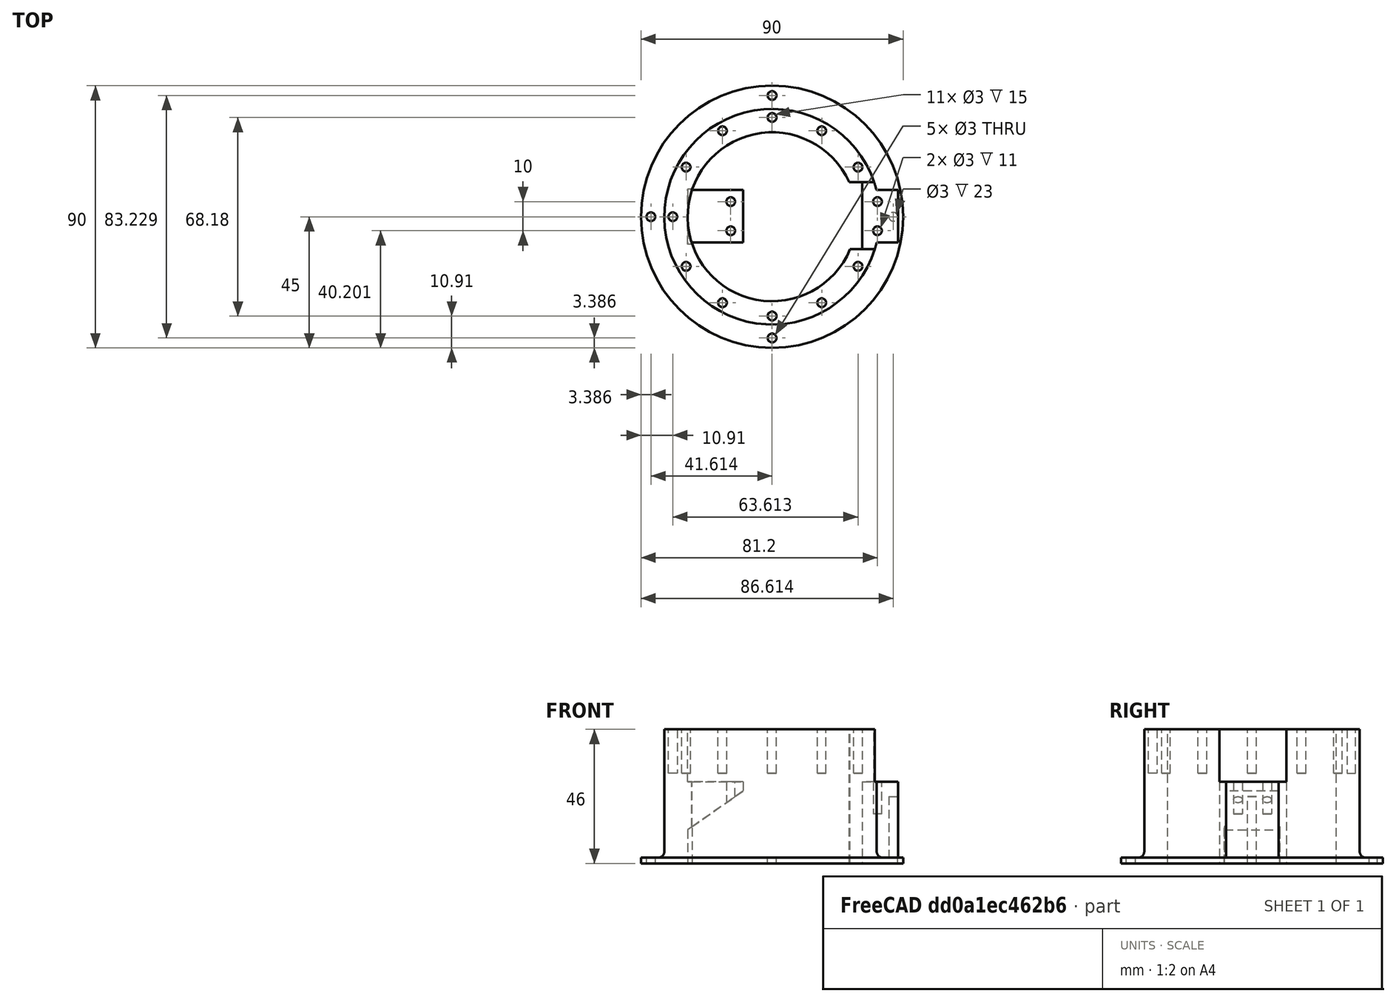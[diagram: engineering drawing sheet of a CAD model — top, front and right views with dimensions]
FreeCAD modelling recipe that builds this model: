
FCSTD DOCUMENT  (FreeCAD 0.20R29177 +426 (Git))
Label: servo_mount_container
License: All rights reserved
LicenseURL: http://en.wikipedia.org/wiki/All_rights_reserved
objects: Sketcher::SketchObject×9, PartDesign::Pocket×6, PartDesign::Pad×3, Mesh::Feature×2, PartDesign::PolarPattern×2, PartDesign::Fillet×1, PartDesign::Body×1
note: 32 computed .brp shape members not serialized (recipe doc carries the construction recipe); baked Part::Feature solids carry a one-line shape summary decoded from their .brp

FEATURE [Mesh::Feature] MG996R_body  label="MG996R-body"
  Placement = pos=(-4,-12,0) rot=(0,1,0;1.5708rad)
FEATURE [Sketcher::SketchObject] Sketch001  label="servo_screw_support"
  AttachmentOffset = pos=(0,0,5) rot=(0,0,1;0rad)
  FullyConstrained = false
  MapMode = 5
  Placement = pos=(0,0,5) rot=(0,0,1;0rad)
  Support = -> [XY_Plane]
  sketch-geometry (4):
    g0: LineSegment StartX=-31.783 StartY=9.16249 StartZ=0 EndX=43.217 EndY=9.16249 EndZ=0
    g1: LineSegment StartX=43.217 StartY=9.16249 StartZ=0 EndX=43.217 EndY=-8.83751 EndZ=0
    g2: LineSegment StartX=43.217 StartY=-8.83751 StartZ=0 EndX=-31.783 EndY=-8.83751 EndZ=0
    g3: LineSegment StartX=-31.783 StartY=-8.83751 StartZ=0 EndX=-31.783 EndY=9.16249 EndZ=0
  constraints (9):
    c: Coincident(g0,g1)
    c: Coincident(g1,g2)
    c: Coincident(g2,g3)
    c: Coincident(g3,g0)
    c: Horizontal(g0)
    c: Horizontal(g2)
    c: Vertical(g1)
    c: DistanceX(g0,g0) = 75
    c: DistanceY(g3,g3) = 18
FEATURE [PartDesign::Pad] Pad  label="servo_support_pad"
  Direction = (0,0,1)
  Length = 28
  Length2 = 10
  Profile = -> Sketch001
  ReferenceAxis = -> Sketch001 [N_Axis]
  Reversed = true
  Type = 0
FEATURE [Mesh::Feature] OuterRace
  Placement = pos=(0,0,32) rot=(0,0,1;0rad)
FEATURE [Sketcher::SketchObject] Sketch004  label="servo_body_insert"
  FullyConstrained = false
  MapMode = 5
  Support = -> [XY_Plane]
  sketch-geometry (4):
    g0: LineSegment StartX=-10 StartY=11.8586 StartZ=0 EndX=31 EndY=11.8586 EndZ=0
    g1: LineSegment StartX=31 StartY=11.8586 StartZ=0 EndX=31 EndY=-11.1414 EndZ=0
    g2: LineSegment StartX=31 StartY=-11.1414 StartZ=0 EndX=-10 EndY=-11.1414 EndZ=0
    g3: LineSegment StartX=-10 StartY=-11.1414 StartZ=0 EndX=-10 EndY=11.8586 EndZ=0
  constraints (11):
    c: Coincident(g0,g1)
    c: Coincident(g1,g2)
    c: Coincident(g2,g3)
    c: Coincident(g3,g0)
    c: Horizontal(g0)
    c: Horizontal(g2)
    c: Vertical(g1)
    c: Vertical(g3)
    c: DistanceX(g0,g0) = 41
    c: DistanceY(g3,g3) = 23
    c: DistanceX(g2,g-1) = 10
FEATURE [Sketcher::SketchObject] Sketch005  label="servo_screw_holes_support"
  AttachmentOffset = pos=(0,0,5) rot=(0,0,1;0rad)
  ExternalGeometry = -> [Sketch004,Sketch001]
  FullyConstrained = false
  MapMode = 5
  Placement = pos=(0,0,5) rot=(0,0,1;0rad)
  Support = -> [XY_Plane]
  sketch-geometry (4):
    g0: LineSegment StartX=31 StartY=11.8586 StartZ=0 EndX=40.0382 EndY=11.8586 EndZ=0
    g1: LineSegment StartX=40.0382 StartY=11.8586 StartZ=0 EndX=40.0382 EndY=-11.1414 EndZ=0
    g2: LineSegment StartX=40.0382 StartY=-11.1414 StartZ=0 EndX=31 EndY=-11.1414 EndZ=0
    g3: LineSegment StartX=31 StartY=-11.1414 StartZ=0 EndX=31 EndY=11.8586 EndZ=0
  constraints (10):
    c: Coincident(g0,g1)
    c: Coincident(g1,g2)
    c: Coincident(g2,g3)
    c: Coincident(g3,g0)
    c: Horizontal(g0)
    c: Horizontal(g2)
    c: Vertical(g1)
    c: Vertical(g3)
    c: Coincident(g0,g-3)
    c: DistanceY(g1,g1) = 23
FEATURE [Sketcher::SketchObject] Sketch006  label="slew_outer_screw_holes"
  AttachmentOffset = pos=(0,0,23) rot=(0,0,1;0rad)
  FullyConstrained = true
  MapMode = 5
  Placement = pos=(0,0,23) rot=(0,0,1;0rad)
  Support = -> [XY_Plane]
  sketch-geometry (1):
    g0: Circle CenterX=-34.09 CenterY=0 CenterZ=0 NormalX=0 NormalY=0 NormalZ=1 AngleXU=0 Radius=1.5
  constraints (3):
    c: PointOnObject(g0,g-1)
    c: Radius(g0) = 1.5
    c: DistanceX(g0,g-1) = 34.09
FEATURE [Sketcher::SketchObject] Sketch007  label="servo_screw_holes"
  AttachmentOffset = pos=(0,0,-6) rot=(0,0,1;0rad)
  FullyConstrained = false
  MapMode = 5
  Placement = pos=(0,0,-6) rot=(0,0,1;0rad)
  Support = -> [XY_Plane]
  sketch-geometry (4):
    g0: Circle CenterX=-14.2 CenterY=5.18693 CenterZ=0 NormalX=0 NormalY=0 NormalZ=1 AngleXU=0 Radius=1.5
    g1: Circle CenterX=-14.2 CenterY=-4.81307 CenterZ=0 NormalX=0 NormalY=0 NormalZ=1 AngleXU=0 Radius=1.5
    g2: Circle CenterX=36.2 CenterY=5.20065 CenterZ=0 NormalX=0 NormalY=0 NormalZ=1 AngleXU=0 Radius=1.5
    g3: Circle CenterX=36.2 CenterY=-4.79935 CenterZ=0 NormalX=0 NormalY=0 NormalZ=1 AngleXU=0 Radius=1.5
  constraints (10):
    c: DistanceX(g0,g-1) = 14.2
    c: Radius(g0) = 1.5
    c: DistanceX(g1,g-1) = 14.2
    c: Radius(g1) = 1.5
    c: DistanceY(g1,g0) = 10
    c: Radius(g3) = 1.5
    c: Radius(g2) = 1.5
    c: DistanceY(g3,g2) = 10
    c: DistanceX(g-1,g2) = 36.2
    c: DistanceX(g-1,g3) = 36.2
FEATURE [Sketcher::SketchObject] Sketch008  label="triangle_spacing_for_servo"
  FullyConstrained = true
  MapMode = 5
  Placement = pos=(0,0,0) rot=(1,0,0;1.5708rad)
  Support = -> [XZ_Plane]
  sketch-geometry (4):
    g0: LineSegment StartX=-9 StartY=2.5 StartZ=0 EndX=-29 EndY=-11.5042 EndZ=0
    g1: LineSegment StartX=-9 StartY=2.5 StartZ=0 EndX=-9 EndY=-24.5 EndZ=0
    g2: LineSegment StartX=-9 StartY=-24.5 StartZ=0 EndX=-29 EndY=-24.5 EndZ=0
    g3: LineSegment StartX=-29 StartY=-11.5042 StartZ=0 EndX=-29 EndY=-24.5 EndZ=0
  constraints (12):
    c: Coincident(g1,g0)
    c: Vertical(g1)
    c: Coincident(g2,g1)
    c: Horizontal(g2)
    c: Coincident(g3,g0)
    c: Coincident(g3,g2)
    c: Vertical(g3)
    c: Angle(g0) = -2.53073
    c: DistanceX(g0,g-1) = 9
    c: DistanceY(g1,g1) = 27
    c: DistanceY(g-1,g0) = 2.5
    c: DistanceX(g2,g2) = 20
FEATURE [Sketcher::SketchObject] Sketch  label="slew_bearing_support_outer"
  AttachmentOffset = pos=(0,0,23) rot=(0,0,1;0rad)
  FullyConstrained = true
  MapMode = 5
  Placement = pos=(0,0,23) rot=(0,0,1;0rad)
  Support = -> [XY_Plane]
  sketch-geometry (2):
    g0: Circle CenterX=0 CenterY=0 CenterZ=0 NormalX=0 NormalY=0 NormalZ=1 AngleXU=0 Radius=37
    g1: Circle CenterX=0 CenterY=0 CenterZ=0 NormalX=0 NormalY=0 NormalZ=1 AngleXU=0 Radius=29
  constraints (4):
    c: Coincident(g0,g-1)
    c: Radius(g0) = 37
    c: Coincident(g1,g0)
    c: Radius(g1) = 29
FEATURE [PartDesign::Pad] Pad001  label="slew_bearing_support_pad"
  BaseFeature = -> Pad
  Direction = (0,0,1)
  Length = 46
  Length2 = 10
  Profile = -> Sketch
  ReferenceAxis = -> Sketch [N_Axis]
  Reversed = true
  Type = 0
FEATURE [PartDesign::Pocket] Pocket001  label="servo_body_cut"
  BaseFeature = -> Pad001
  Direction = (0,0,-1)
  Length = 5
  Length2 = 5
  Midplane = true
  Profile = -> Sketch004
  ReferenceAxis = -> Sketch004 [N_Axis]
  Type = 1
FEATURE [PartDesign::Pocket] Pocket002  label="screw_holes"
  BaseFeature = -> Pocket001
  Direction = (0,0,-1)
  Length = 5
  Length2 = 5
  Profile = -> Sketch005
  ReferenceAxis = -> Sketch005 [N_Axis]
  Reversed = true
  Type = 1
FEATURE [PartDesign::Pocket] Pocket003  label="slew_outer_holes_pocket"
  BaseFeature = -> Pocket002
  Direction = (0,0,-1)
  Length = 15
  Length2 = 5
  Profile = -> Sketch006
  ReferenceAxis = -> Sketch006 [N_Axis]
  Type = 0
FEATURE [PartDesign::PolarPattern] PolarPattern  label="slew_bearing_screw_holes_12"
  Angle = 360
  Axis = -> Sketch006 [N_Axis]
  BaseFeature = -> Pocket003
  Occurrences = 12
  Originals = -> [Pocket003]
FEATURE [PartDesign::Pocket] Pocket004  label="screw_holes_servo_pocket"
  BaseFeature = -> PolarPattern
  Direction = (0,0,-1)
  Length = 5
  Length2 = 5
  Profile = -> Sketch007
  ReferenceAxis = -> Sketch007 [N_Axis]
  Reversed = true
  Type = 1
FEATURE [PartDesign::Pocket] Pocket006  label="trianle_cut"
  BaseFeature = -> Pocket004
  Direction = (0,1,2e-16)
  Length = 19
  Length2 = 5
  Midplane = true
  Profile = -> Sketch008
  ReferenceAxis = -> Sketch008 [N_Axis]
  Type = 0
FEATURE [Sketcher::SketchObject] Sketch009  label="base_support"
  AttachmentOffset = pos=(0,0,-23) rot=(0,0,1;0rad)
  FullyConstrained = true
  MapMode = 5
  Placement = pos=(0,0,-23) rot=(0,0,1;0rad)
  Support = -> [XY_Plane]
  sketch-geometry (2):
    g0: Circle CenterX=0 CenterY=0 CenterZ=0 NormalX=0 NormalY=0 NormalZ=1 AngleXU=0 Radius=37
    g1: Circle CenterX=0 CenterY=0 CenterZ=0 NormalX=0 NormalY=0 NormalZ=1 AngleXU=0 Radius=45
  constraints (4):
    c: Coincident(g0,g-1)
    c: Radius(g0) = 37
    c: Coincident(g1,g0)
    c: Radius(g1) = 45
FEATURE [PartDesign::Pad] Pad002  label="base_support_pad"
  BaseFeature = -> Pocket006
  Direction = (0,0,1)
  Length = 2
  Length2 = 10
  Profile = -> Sketch009
  ReferenceAxis = -> Sketch009 [N_Axis]
  Type = 0
FEATURE [Sketcher::SketchObject] Sketch010  label="base_support_scew"
  FullyConstrained = false
  MapMode = 5
  Support = -> [XY_Plane]
  sketch-geometry (1):
    g0: Circle CenterX=-41.6144 CenterY=0 CenterZ=0 NormalX=0 NormalY=0 NormalZ=1 AngleXU=0 Radius=1.5
  constraints (2):
    c: PointOnObject(g0,g-1)
    c: Radius(g0) = 1.5
FEATURE [PartDesign::Pocket] Pocket
  BaseFeature = -> Pad002
  Direction = (0,0,-1)
  Length = 5
  Length2 = 5
  Profile = -> Sketch010
  ReferenceAxis = -> Sketch010 [N_Axis]
  Type = 1
FEATURE [PartDesign::PolarPattern] PolarPattern001
  Angle = 360
  Axis = -> Sketch010 [N_Axis]
  BaseFeature = -> Pocket
  Occurrences = 4
  Originals = -> [Pocket]
FEATURE [PartDesign::Fillet] Fillet
  Base = -> PolarPattern001 [Edge101]
  BaseFeature = -> PolarPattern001
  Radius = 2
  SupportTransform = false
  UseAllEdges = false
FEATURE [PartDesign::Body] Body
  Group = -> [Sketch001,Pad,Sketch,Pad001,Sketch004,Pocket001,Sketch005,Pocket002,Sketch006,Pocket003,PolarPattern,Sketch007,Pocket004,Sketch008,Pocket006,Sketch009,Pad002,Sketch010,Pocket,PolarPattern001,Fillet]
  Origin = -> Origin
  Tip = -> Fillet
